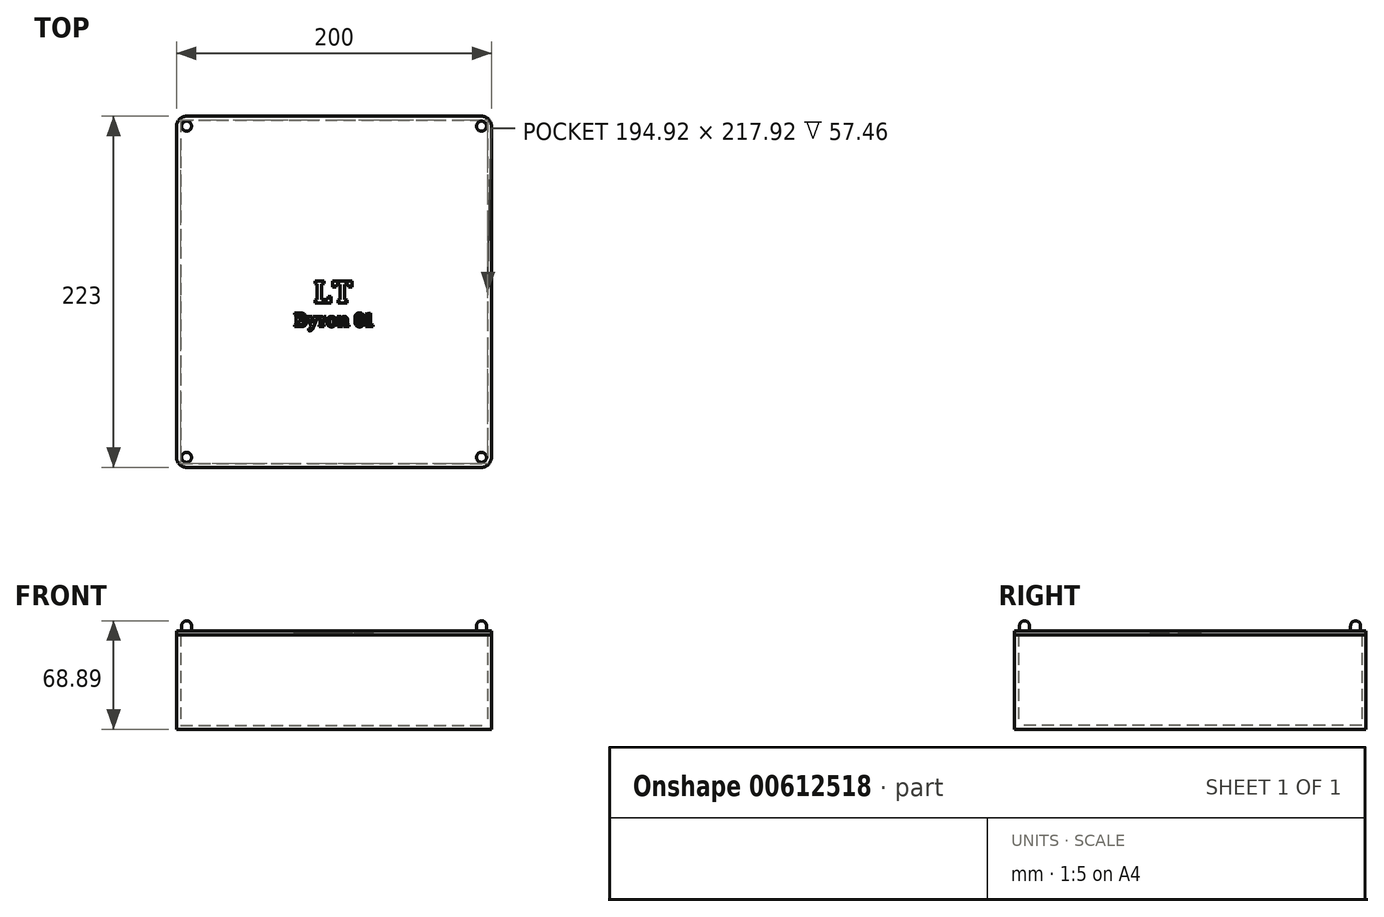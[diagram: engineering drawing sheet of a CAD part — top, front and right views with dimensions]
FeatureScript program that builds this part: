
annotation { "Feature Type Name" : "Feature", "Feature Type Description" : "" }
export const myFeature = defineFeature(function(context is Context, id is Id, definition is map)
    precondition{}
    {
        {
            var Q0;
            Q0=qCreatedBy(makeId("Top.planeOp"),FACE);
            var sketch = newSketch(context, id + "F0", { "sketchPlane" : qUnion([Q0])});
            skLineSegment(sketch, "E0.bottom", {"start": v(-100, 111.5) * mm, "end": v(100, 111.5) * mm});
            skLineSegment(sketch, "E0.top", {"start": v(-100, -111.5) * mm, "end": v(100, -111.5) * mm});
            skLineSegment(sketch, "E0.left", {"start": v(-100, 111.5) * mm, "end": v(-100, -111.5) * mm});
            skLineSegment(sketch, "E0.right", {"start": v(100, 111.5) * mm, "end": v(100, -111.5) * mm});
            skPoint(sketch, "E1", {"position": v(100, 0) * mm});
            skPoint(sketch, "E2", {"position": v(0, -111.5) * mm});
            skSolve(sketch);
        }
        {
            var Q0;
            Q0 = qSketchRegion(id + "F0", true);
            extrude(context, id + "F1", {"entities" : qUnion([Q0]), "depth" : 60 * mm, "offsetDistance" : 25.4 * mm});
        }
        {
            var Q0;
            Q0=makeQuery(id+"F1.opExtrude","CAP_FACE",FACE,{"disambiguationData":[OSD([sQuery(id+"F0.wireOp",EDGE,"E0.bottom"),sQuery(id+"F0.wireOp",EDGE,"E0.top"),sQuery(id+"F0.wireOp",EDGE,"E0.left"),sQuery(id+"F0.wireOp",EDGE,"E0.right")])],"isStart":false});
            shell(context, id + "F2", {"entities" : qUnion([Q0]), "thickness" : 2.54 * mm});
        }
        {
            var Q0;
            Q0=makeQuery(id+"F1.opExtrude","CAP_FACE",FACE,{"disambiguationData":[OSD([sQuery(id+"F0.wireOp",EDGE,"E0.bottom"),sQuery(id+"F0.wireOp",EDGE,"E0.top"),sQuery(id+"F0.wireOp",EDGE,"E0.left"),sQuery(id+"F0.wireOp",EDGE,"E0.right")])],"isStart":false});
            var sketch = newSketch(context, id + "F3", { "sketchPlane" : qUnion([Q0])});
            skLineSegment(sketch, "E3.bottom", {"start": v(-100, 111.5) * mm, "end": v(100, 111.5) * mm});
            skLineSegment(sketch, "E3.top", {"start": v(-100, -111.5) * mm, "end": v(100, -111.5) * mm});
            skLineSegment(sketch, "E3.left", {"start": v(-100, 111.5) * mm, "end": v(-100, -111.5) * mm});
            skLineSegment(sketch, "E3.right", {"start": v(100, 111.5) * mm, "end": v(100, -111.5) * mm});
            skSolve(sketch);
        }
        {
            var Q0;
            Q0 = qSketchRegion(id + "F3", true);
            extrude(context, id + "F4", {"entities" : qUnion([Q0]), "depth" : 2.54 * mm, "offsetDistance" : 25.4 * mm});
        }
        {
            var Q0;
            Q0=makeQuery(id+"F1.opExtrude","SWEPT_EDGE",EDGE,{"disambiguationData":[OSD([sQuery(id+"F0.wireOp",EDGE,"E0.top"),sQuery(id+"F0.wireOp",EDGE,"E0.right")])]});
            var Q1;
            Q1=makeQuery(id+"F1.opExtrude","SWEPT_EDGE",EDGE,{"disambiguationData":[OSD([sQuery(id+"F0.wireOp",EDGE,"E0.bottom"),sQuery(id+"F0.wireOp",EDGE,"E0.right")])]});
            var Q2;
            Q2=makeQuery(id+"F4.opExtrude","SWEPT_EDGE",EDGE,{"disambiguationData":[OSD([sQuery(id+"F3.wireOp",EDGE,"E3.bottom"),sQuery(id+"F3.wireOp",EDGE,"E3.right")])]});
            var Q3;
            Q3=makeQuery(id+"F4.opExtrude","SWEPT_EDGE",EDGE,{"disambiguationData":[OSD([sQuery(id+"F3.wireOp",EDGE,"E3.top"),sQuery(id+"F3.wireOp",EDGE,"E3.right")])]});
            var Q4;
            Q4=makeQuery(id+"F1.opExtrude","SWEPT_EDGE",EDGE,{"disambiguationData":[OSD([sQuery(id+"F0.wireOp",EDGE,"E0.top"),sQuery(id+"F0.wireOp",EDGE,"E0.left")])]});
            var Q5;
            Q5=makeQuery(id+"F4.opExtrude","SWEPT_EDGE",EDGE,{"disambiguationData":[OSD([sQuery(id+"F3.wireOp",EDGE,"E3.top"),sQuery(id+"F3.wireOp",EDGE,"E3.left")])]});
            var Q6;
            Q6=makeQuery(id+"F1.opExtrude","SWEPT_EDGE",EDGE,{"disambiguationData":[OSD([sQuery(id+"F0.wireOp",EDGE,"E0.bottom"),sQuery(id+"F0.wireOp",EDGE,"E0.left")])]});
            var Q7;
            Q7=makeQuery(id+"F4.opExtrude","SWEPT_EDGE",EDGE,{"disambiguationData":[OSD([sQuery(id+"F3.wireOp",EDGE,"E3.bottom"),sQuery(id+"F3.wireOp",EDGE,"E3.left")])]});
            fillet(context, id + "F5", {"entities" : qUnion([Q0, Q1, Q2, Q3, Q4, Q5, Q6, Q7]), "radius" : 6.35 * mm, "tangentPropagation" : true, "allowEdgeOverflow" : false});
        }
        {
            var Q0;
            Q0=makeQuery(id+"F4.opExtrude","CAP_FACE",FACE,{"disambiguationData":[OSD([sQuery(id+"F3.wireOp",EDGE,"E3.bottom"),sQuery(id+"F3.wireOp",EDGE,"E3.top"),sQuery(id+"F3.wireOp",EDGE,"E3.left"),sQuery(id+"F3.wireOp",EDGE,"E3.right")])],"isStart":false});
            var sketch = newSketch(context, id + "F6", { "sketchPlane" : qUnion([Q0])});
            skText(sketch, "E4", { "text": "LT", "fontName": "RobotoSlab-Bold.ttf"});
            skPoint(sketch, "E5", {"position": v(0, 0) * mm});
            skText(sketch, "E6", { "text": "Byron 01", "fontName": "RobotoSlab-Bold.ttf"});
            skLineSegment(sketch, "E7", {"start": v(0, 0) * mm, "end": v(0, -38.89) * mm, "construction": true});
            const initialGuessF6  = {"E4": [-0.0127, -0.00703, 1, 0, 0.01406], "E6": [-0.0254, -0.02217, 1, 0, 0.00879]};
            skSetInitialGuess(sketch, initialGuessF6);
            skSolve(sketch);
        }
        {
            var Q0;
            Q0 = qSketchRegion(id + "F6", true);
            extrude(context, id + "F7", {"entities" : qUnion([Q0]), "operationType" : NewBodyOperationType.REMOVE, "oppositeDirection" : true, "depth" : 1.27 * mm, "offsetDistance" : 25.4 * mm});
        }
        {
            var Q0;
            {var subQ0=sQuery(id+"F3.wireOp",EDGE,"E3.left");var subQ1=sQuery(id+"F3.wireOp",EDGE,"E3.top");var subQ2=sQuery(id+"F3.wireOp",EDGE,"E3.right");var subQ3=sQuery(id+"F3.wireOp",EDGE,"E3.bottom");Q0=makeQuery(id+"F7.boolean.opBoolean","SPLIT",FACE,{"disambiguationData":[TD([makeQuery(id+"F4.opExtrude","SWEPT_FACE",FACE,{"disambiguationData":[OSD([subQ3])]})])],"derivedFrom":makeQuery(id+"F4.opExtrude","CAP_FACE",FACE,{"disambiguationData":[OSD([subQ3,subQ1,subQ0,subQ2])],"isStart":false})});}
            var sketch = newSketch(context, id + "F8", { "sketchPlane" : qUnion([Q0])});
            skLineSegment(sketch, "E8", {"start": v(-98.14, 109.64) * mm, "end": v(98.14, -109.64) * mm, "construction": true});
            skLineSegment(sketch, "E9", {"start": v(98.14, -109.64) * mm, "end": v(-98.14, -109.64) * mm, "construction": true});
            skLineSegment(sketch, "E10", {"start": v(-98.14, -109.64) * mm, "end": v(98.14, 109.64) * mm, "construction": true});
            skArc(sketch, "E11", {"start": v(100, 105.15) * mm, "mid": v(98.14, 109.64) * mm, "end": v(93.65, 111.5) * mm, "construction": true});
            skCircle(sketch, "E12", {"center": v(93.65, 105.15) * mm, "radius": 3.18 * mm});
            skLineSegment(sketch, "E13", {"start": v(0, 0) * mm, "end": v(0, 7.66) * mm, "construction": true});
            skLineSegment(sketch, "E14", {"start": v(0, 0) * mm, "end": v(8.14, 0) * mm, "construction": true});
            skCircle(sketch, "E15.MirrorC", {"center": v(-93.65, 105.15) * mm, "radius": 3.18 * mm});
            skCircle(sketch, "E16.MirrorC", {"center": v(93.65, -105.15) * mm, "radius": 3.18 * mm});
            skCircle(sketch, "E17.MirrorC", {"center": v(-93.65, -105.15) * mm, "radius": 3.18 * mm});
            skArc(sketch, "E18.MirrorCS", {"start": v(100, -105.15) * mm, "mid": v(98.14, -109.64) * mm, "end": v(93.65, -111.5) * mm, "construction": true});
            skSolve(sketch);
        }
        {
            var Q0;
            Q0 = qSketchRegion(id + "F8", true);
            extrude(context, id + "F9", {"entities" : qUnion([Q0]), "operationType" : NewBodyOperationType.ADD, "depth" : 6.35 * mm, "offsetDistance" : 25.4 * mm});
        }
        {
            var Q0;
            Q0=makeQuery(id+"F9.opExtrude","CAP_FACE",FACE,{"disambiguationData":[OSD([sQuery(id+"F8.wireOp",EDGE,"E17.MirrorC")])],"isStart":false});
            var Q1;
            Q1=makeQuery(id+"F9.opExtrude","CAP_FACE",FACE,{"disambiguationData":[OSD([sQuery(id+"F8.wireOp",EDGE,"E16.MirrorC")])],"isStart":false});
            var Q2;
            Q2=makeQuery(id+"F9.opExtrude","CAP_FACE",FACE,{"disambiguationData":[OSD([sQuery(id+"F8.wireOp",EDGE,"E12")])],"isStart":false});
            var Q3;
            Q3=makeQuery(id+"F9.opExtrude","CAP_FACE",FACE,{"disambiguationData":[OSD([sQuery(id+"F8.wireOp",EDGE,"E15.MirrorC")])],"isStart":false});
            fillet(context, id + "F10", {"entities" : qUnion([Q0, Q1, Q2, Q3]), "radius" : 3.17 * mm, "tangentPropagation" : true, "allowEdgeOverflow" : false});
        }
    });
